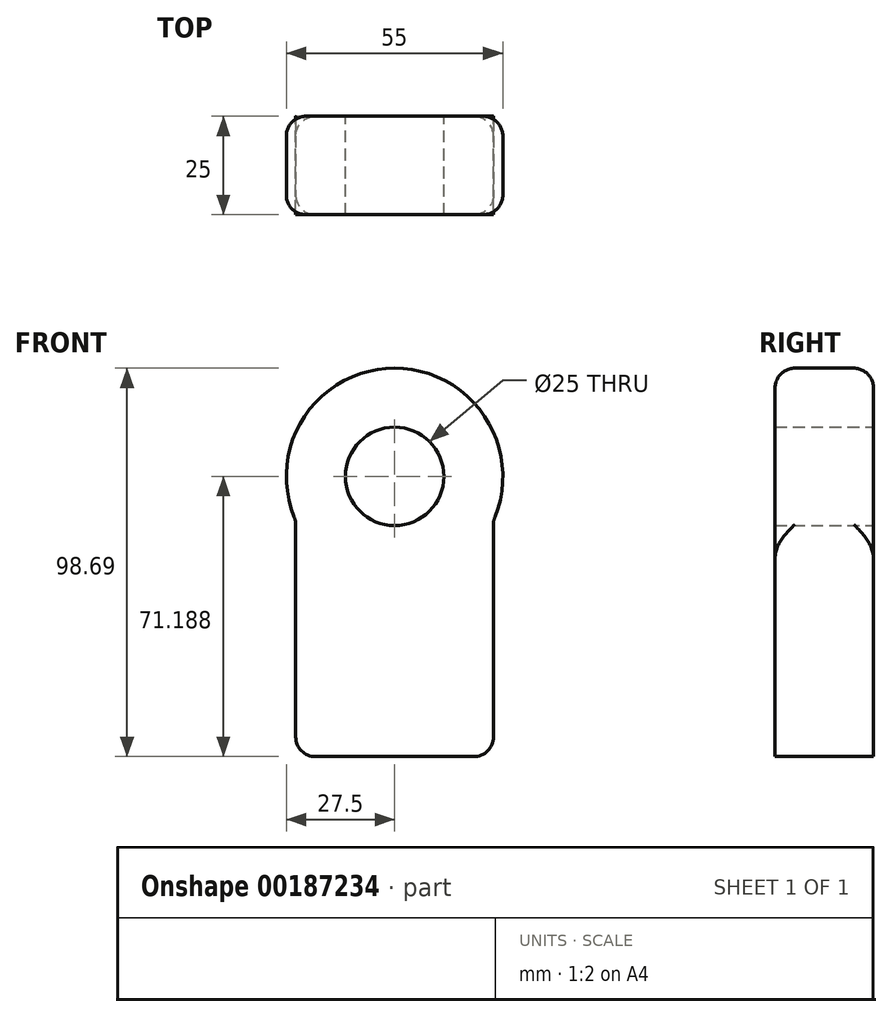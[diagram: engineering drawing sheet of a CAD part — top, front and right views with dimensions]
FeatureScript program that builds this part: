
annotation { "Feature Type Name" : "Feature", "Feature Type Description" : "" }
export const myFeature = defineFeature(function(context is Context, id is Id, definition is map)
    precondition{}
    {
        {
            var Q0;
            Q0=qCreatedBy(makeId("Front.planeOp"),FACE);
            var sketch = newSketch(context, id + "F0", { "sketchPlane" : qUnion([Q0])});
            skLineSegment(sketch, "E0", {"start": v(-25.12, 18.38) * mm, "end": v(-25.12, -41.62) * mm});
            skLineSegment(sketch, "E1", {"start": v(-25.12, -41.62) * mm, "end": v(25.12, -41.62) * mm});
            skLineSegment(sketch, "E2", {"start": v(25.12, -41.62) * mm, "end": v(25.12, 18.38) * mm});
            skArc(sketch, "E3", {"start": v(25.12, 18.38) * mm, "mid": v(0, 57.07) * mm, "end": v(-25.12, 18.38) * mm});
            skCircle(sketch, "E4", {"center": v(0, 29.57) * mm, "radius": 12.5 * mm});
            skSolve(sketch);
        }
        {
            var Q0;
            Q0=makeQuery(id+"F0.imprint","IMPRINT",FACE,{"disambiguationData":[TD([[makeQuery(id+"F0.imprint","IMPRINT",EDGE,{"derivedFrom":sQuery(id+"F0.wireOp",EDGE,"E0")}),1.0]])]});
            extrude(context, id + "F1", {"entities" : qUnion([Q0]), "depth" : 25 * mm});
        }
        {
            var Q0;
            Q0=makeQuery(id+"F1.opExtrude","SWEPT_EDGE",EDGE,{"disambiguationData":[OSD([sQuery(id+"F0.wireOp",EDGE,"E0"),sQuery(id+"F0.wireOp",EDGE,"E1")])]});
            var Q1;
            Q1=makeQuery(id+"F1.opExtrude","SWEPT_EDGE",EDGE,{"disambiguationData":[OSD([sQuery(id+"F0.wireOp",EDGE,"E1"),sQuery(id+"F0.wireOp",EDGE,"E2")])]});
            var Q2;
            Q2=makeQuery(id+"F1.opExtrude","SWEPT_EDGE",EDGE,{"disambiguationData":[OSD([sQuery(id+"F0.wireOp",EDGE,"E0"),sQuery(id+"F0.wireOp",EDGE,"E3")])]});
            var Q3;
            Q3=makeQuery(id+"F1.opExtrude","SWEPT_FACE",FACE,{"disambiguationData":[OSD([sQuery(id+"F0.wireOp",EDGE,"E3")])]});
            fillet(context, id + "F2", {"entities" : qUnion([Q0, Q1, Q2, Q3]), "radius" : 5 * mm, "tangentPropagation" : true, "allowEdgeOverflow" : false});
        }
    });
